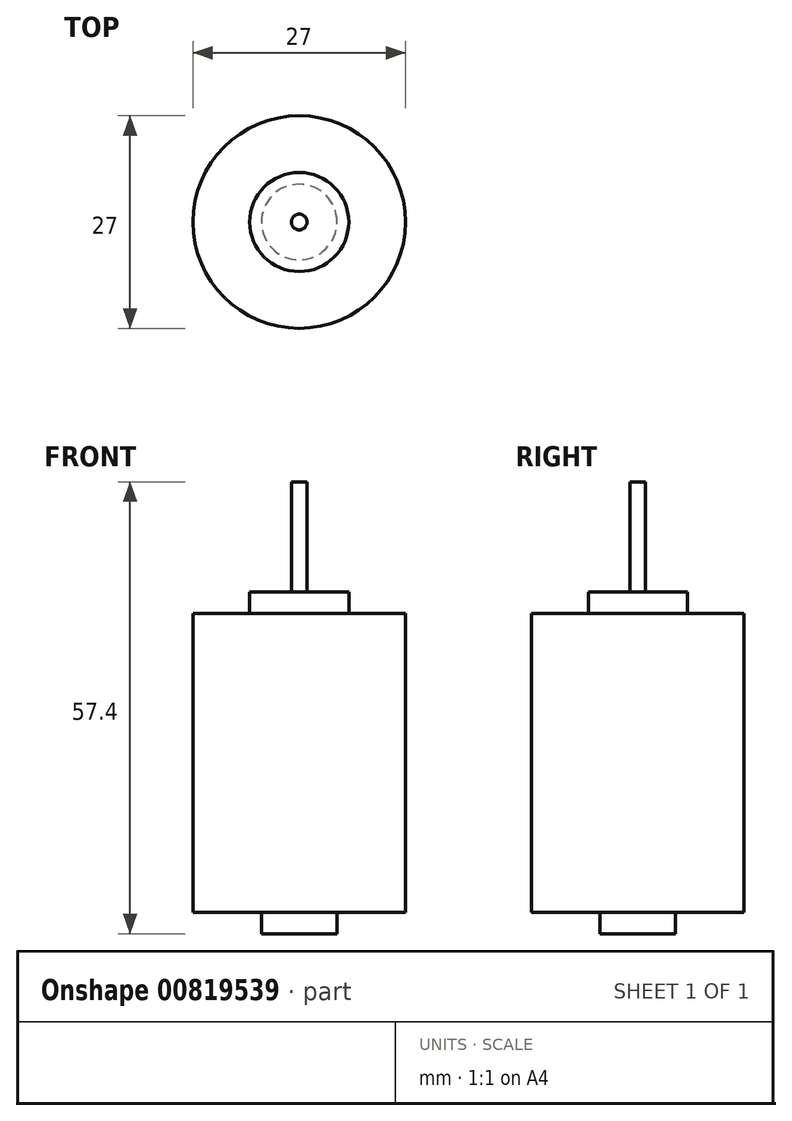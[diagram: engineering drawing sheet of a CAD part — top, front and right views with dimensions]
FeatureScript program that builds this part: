
annotation { "Feature Type Name" : "Feature", "Feature Type Description" : "" }
export const myFeature = defineFeature(function(context is Context, id is Id, definition is map)
    precondition{}
    {
        {
            var Q0;
            Q0=qCreatedBy(makeId("Right.planeOp"),FACE);
            var sketch = newSketch(context, id + "F0", { "sketchPlane" : qUnion([Q0])});
            skLineSegment(sketch, "E0", {"start": v(25.17, 0.27) * mm, "end": v(29.97, 0.27) * mm});
            skLineSegment(sketch, "E1", {"start": v(29.97, 0.27) * mm, "end": v(29.97, 2.97) * mm});
            skLineSegment(sketch, "E2", {"start": v(29.97, 2.97) * mm, "end": v(38.67, 2.97) * mm});
            skLineSegment(sketch, "E3", {"start": v(38.67, 2.97) * mm, "end": v(38.67, 40.97) * mm});
            skLineSegment(sketch, "E4", {"start": v(38.67, 40.97) * mm, "end": v(31.47, 40.97) * mm});
            skLineSegment(sketch, "E5", {"start": v(31.47, 40.97) * mm, "end": v(31.47, 43.67) * mm});
            skLineSegment(sketch, "E6", {"start": v(31.47, 43.67) * mm, "end": v(26.17, 43.67) * mm});
            skLineSegment(sketch, "E7", {"start": v(26.17, 43.67) * mm, "end": v(26.17, 57.67) * mm});
            skLineSegment(sketch, "E8", {"start": v(26.17, 57.67) * mm, "end": v(25.17, 57.67) * mm});
            skLineSegment(sketch, "E9", {"start": v(25.17, 57.67) * mm, "end": v(25.17, 0.27) * mm});
            skSolve(sketch);
        }
        {
            var Q0;
            Q0=makeQuery(id+"F0.imprint","IMPRINT",FACE,{"disambiguationData":[TD([[makeQuery(id+"F0.imprint","IMPRINT",EDGE,{"derivedFrom":sQuery(id+"F0.wireOp",EDGE,"E0")}),1.0]])]});
            var Q1;
            Q1=sQuery(id+"F0.wireOp",EDGE,"E9");
            revolve(context, id + "F1", {"surfaceOperationType" : NewSurfaceOperationType.NEW, "entities" : qUnion([Q0]), "axis" : qUnion([Q1]), "revolveType" : RevolveType.FULL});
        }
    });
